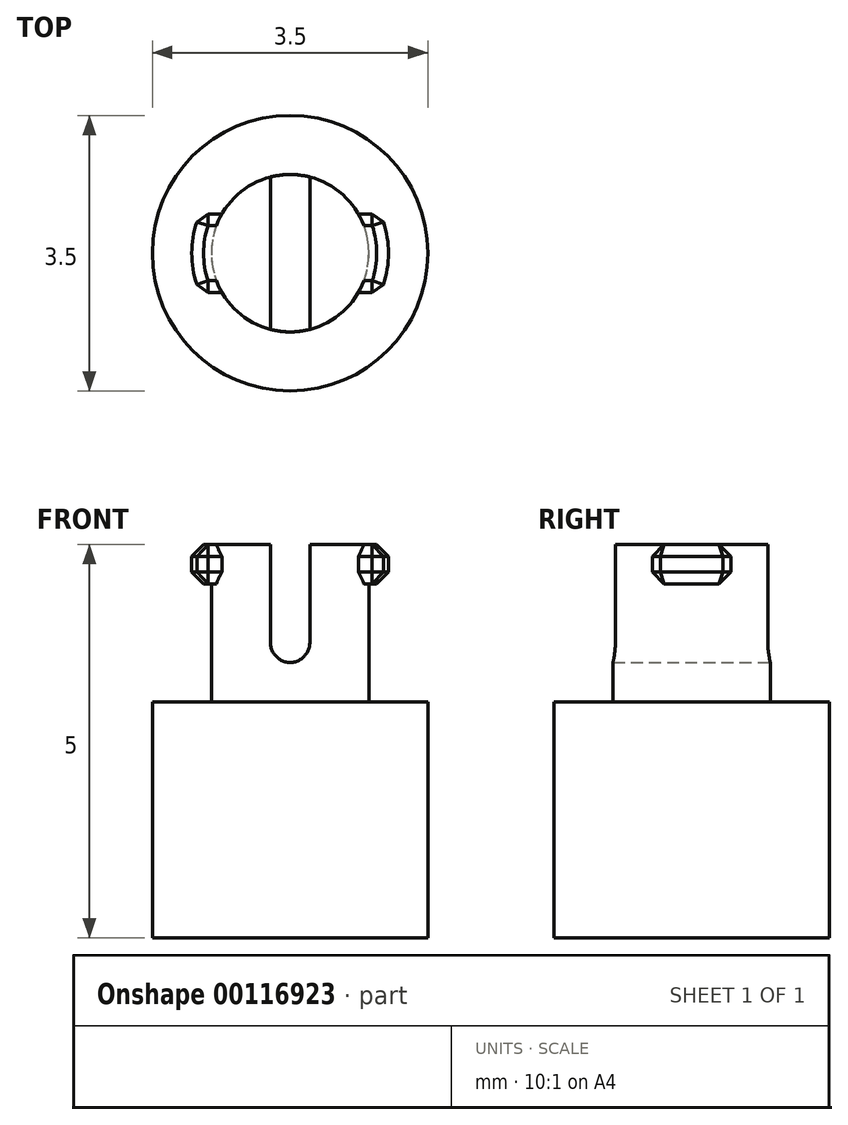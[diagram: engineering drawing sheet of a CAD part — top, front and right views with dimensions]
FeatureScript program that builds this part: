
annotation { "Feature Type Name" : "Feature", "Feature Type Description" : "" }
export const myFeature = defineFeature(function(context is Context, id is Id, definition is map)
    precondition{}
    {
        {
            var Q0;
            Q0=qCreatedBy(makeId("Top.planeOp"),FACE);
            var sketch = newSketch(context, id + "F0", { "sketchPlane" : qUnion([Q0])});
            skCircle(sketch, "E0", {"center": v(0, 0) * mm, "radius": 1 * mm});
            skCircle(sketch, "E1", {"center": v(0, 0) * mm, "radius": 1.75 * mm});
            skSolve(sketch);
        }
        {
            var Q0;
            Q0=makeQuery(id+"F0.imprint","IMPRINT",FACE,{"disambiguationData":[TD([[makeQuery(id+"F0.imprint","IMPRINT",EDGE,{"derivedFrom":sQuery(id+"F0.wireOp",EDGE,"E0")}),-1.0]])]});
            extrude(context, id + "F1", {"entities" : qUnion([Q0]), "depth" : 3 * mm});
        }
        {
            var Q0;
            Q0=makeQuery(id+"F0.imprint","IMPRINT",FACE,{"disambiguationData":[TD([[makeQuery(id+"F0.imprint","IMPRINT",EDGE,{"derivedFrom":sQuery(id+"F0.wireOp",EDGE,"E0")}),1.0]])]});
            extrude(context, id + "F2", {"entities" : qUnion([Q0]), "operationType" : NewBodyOperationType.ADD, "depth" : 5 * mm});
        }
        {
            var Q0;
            {var subQ0=sQuery(id+"F0.wireOp",EDGE,"E0");Q0=makeQuery(id+"F7.boolean.opBoolean","SPLIT",FACE,{"disambiguationData":[TD([makeQuery(id+"F7.opExtrude","SWEPT_FACE",FACE,{"disambiguationData":[OSD([sQuery(id+"F4.wireOp",EDGE,"E6.left")])]})])],"derivedFrom":makeQuery(id+"F2.opExtrude","CAP_FACE",FACE,{"disambiguationData":[OSD([subQ0])],"isStart":false})});}
            var sketch = newSketch(context, id + "F3", { "sketchPlane" : qUnion([Q0])});
            skArc(sketch, "E2", {"start": v(1.15, -0.5) * mm, "mid": v(1.25, 0) * mm, "end": v(1.15, 0.5) * mm});
            skLineSegment(sketch, "E3.bottom", {"start": v(-1.15, -0.5) * mm, "end": v(1.15, -0.5) * mm});
            skLineSegment(sketch, "E3.top", {"start": v(-1.15, 0.5) * mm, "end": v(1.15, 0.5) * mm});
            skArc(sketch, "E4.trimOffspring", {"start": v(-1.15, 0.5) * mm, "mid": v(-1.25, 0) * mm, "end": v(-1.15, -0.5) * mm});
            skPoint(sketch, "E3.left.end.orphan", {"position": v(-1.5, 0.5) * mm});
            skPoint(sketch, "E5.orphan", {"position": v(-1.5, -0.5) * mm});
            skPoint(sketch, "E3.right.end.orphan", {"position": v(1.5, 0.5) * mm});
            skPoint(sketch, "E3.right.start.orphan", {"position": v(1.5, -0.5) * mm});
            skSolve(sketch);
        }
        {
            var Q0;
            Q0=qCreatedBy(makeId("Top.planeOp"),FACE);
            var sketch = newSketch(context, id + "F4", { "sketchPlane" : qUnion([Q0])});
            skLineSegment(sketch, "E6.bottom", {"start": v(-0.25, 2.5) * mm, "end": v(0.25, 2.5) * mm});
            skLineSegment(sketch, "E6.top", {"start": v(-0.25, -2.5) * mm, "end": v(0.25, -2.5) * mm});
            skLineSegment(sketch, "E6.left", {"start": v(-0.25, 2.5) * mm, "end": v(-0.25, -2.5) * mm});
            skLineSegment(sketch, "E6.right", {"start": v(0.25, 2.5) * mm, "end": v(0.25, -2.5) * mm});
            skPoint(sketch, "E6.middle", {"position": v(0, 0) * mm});
            skSolve(sketch);
        }
        {
            var Q0;
            Q0 = qSketchRegion(id + "F3", true);
            extrude(context, id + "F5", {"entities" : qUnion([Q0]), "operationType" : NewBodyOperationType.ADD, "oppositeDirection" : true, "depth" : 0.5 * mm});
        }
        {
            var Q0;
            Q0=makeQuery(id+"F5.opExtrude","CAP_EDGE",EDGE,{"disambiguationData":[OSD([sQuery(id+"F3.wireOp",EDGE,"E4.trimOffspring")])],"isStart":false});
            var Q1;
            {var subQ0=sQuery(id+"F3.wireOp",EDGE,"E4.trimOffspring");var subQ1=sQuery(id+"F3.wireOp",EDGE,"E3.top");Q1=makeQuery(id+"F5.boolean.opBoolean","SPLIT",EDGE,{"disambiguationData":[TD([makeQuery(id+"F5.opExtrude","SWEPT_FACE",FACE,{"disambiguationData":[OSD([subQ0])]})])],"derivedFrom":makeQuery(id+"F5.opExtrude","CAP_EDGE",EDGE,{"disambiguationData":[OSD([subQ1])],"isStart":false})});}
            var Q2;
            {var subQ0=sQuery(id+"F3.wireOp",EDGE,"E4.trimOffspring");var subQ1=sQuery(id+"F3.wireOp",EDGE,"E3.bottom");Q2=makeQuery(id+"F5.boolean.opBoolean","SPLIT",EDGE,{"disambiguationData":[TD([makeQuery(id+"F5.opExtrude","SWEPT_FACE",FACE,{"disambiguationData":[OSD([subQ0])]})])],"derivedFrom":makeQuery(id+"F5.opExtrude","CAP_EDGE",EDGE,{"disambiguationData":[OSD([subQ1])],"isStart":false})});}
            var Q3;
            Q3=makeQuery(id+"F5.opExtrude","SWEPT_EDGE",EDGE,{"disambiguationData":[OSD([sQuery(id+"F3.wireOp",EDGE,"E3.top"),sQuery(id+"F3.wireOp",EDGE,"E4.trimOffspring")])]});
            var Q4;
            Q4=makeQuery(id+"F5.opExtrude","SWEPT_EDGE",EDGE,{"disambiguationData":[OSD([sQuery(id+"F3.wireOp",EDGE,"E3.bottom"),sQuery(id+"F3.wireOp",EDGE,"E4.trimOffspring")])]});
            var Q5;
            Q5=makeQuery(id+"F5.opExtrude","CAP_EDGE",EDGE,{"disambiguationData":[OSD([sQuery(id+"F3.wireOp",EDGE,"E2")])],"isStart":false});
            var Q6;
            Q6=makeQuery(id+"F5.opExtrude","SWEPT_EDGE",EDGE,{"disambiguationData":[OSD([sQuery(id+"F3.wireOp",EDGE,"E2"),sQuery(id+"F3.wireOp",EDGE,"E3.top")])]});
            var Q7;
            {var subQ0=sQuery(id+"F3.wireOp",EDGE,"E2");var subQ1=sQuery(id+"F3.wireOp",EDGE,"E3.top");Q7=makeQuery(id+"F5.boolean.opBoolean","SPLIT",EDGE,{"disambiguationData":[TD([makeQuery(id+"F5.opExtrude","SWEPT_FACE",FACE,{"disambiguationData":[OSD([subQ0])]})])],"derivedFrom":makeQuery(id+"F5.opExtrude","CAP_EDGE",EDGE,{"disambiguationData":[OSD([subQ1])],"isStart":false})});}
            var Q8;
            Q8=makeQuery(id+"F5.opExtrude","SWEPT_EDGE",EDGE,{"disambiguationData":[OSD([sQuery(id+"F3.wireOp",EDGE,"E2"),sQuery(id+"F3.wireOp",EDGE,"E3.bottom")])]});
            var Q9;
            {var subQ0=sQuery(id+"F3.wireOp",EDGE,"E2");var subQ1=sQuery(id+"F3.wireOp",EDGE,"E3.bottom");Q9=makeQuery(id+"F5.boolean.opBoolean","SPLIT",EDGE,{"disambiguationData":[TD([makeQuery(id+"F5.opExtrude","SWEPT_FACE",FACE,{"disambiguationData":[OSD([subQ0])]})])],"derivedFrom":makeQuery(id+"F5.opExtrude","CAP_EDGE",EDGE,{"disambiguationData":[OSD([subQ1])],"isStart":false})});}
            var Q10;
            Q10=makeQuery(id+"F5.opExtrude","CAP_EDGE",EDGE,{"disambiguationData":[OSD([sQuery(id+"F3.wireOp",EDGE,"E4.trimOffspring")])],"isStart":true});
            var Q11;
            Q11=makeQuery(id+"F5.opExtrude","CAP_EDGE",EDGE,{"disambiguationData":[OSD([sQuery(id+"F3.wireOp",EDGE,"E2")])],"isStart":true});
            var Q12;
            {var subQ0=sQuery(id+"F3.wireOp",EDGE,"E3.bottom");var subQ1=sQuery(id+"F3.wireOp",EDGE,"E2");Q12=makeQuery(id+"F5.boolean.opBoolean","SPLIT",EDGE,{"disambiguationData":[TD([makeQuery(id+"F5.opExtrude","SWEPT_FACE",FACE,{"disambiguationData":[OSD([subQ1])]})])],"derivedFrom":makeQuery(id+"F5.opExtrude","CAP_EDGE",EDGE,{"disambiguationData":[OSD([subQ0])],"isStart":true})});}
            var Q13;
            {var subQ0=sQuery(id+"F3.wireOp",EDGE,"E3.bottom");var subQ1=sQuery(id+"F3.wireOp",EDGE,"E4.trimOffspring");Q13=makeQuery(id+"F5.boolean.opBoolean","SPLIT",EDGE,{"disambiguationData":[TD([makeQuery(id+"F5.opExtrude","SWEPT_FACE",FACE,{"disambiguationData":[OSD([subQ1])]})])],"derivedFrom":makeQuery(id+"F5.opExtrude","CAP_EDGE",EDGE,{"disambiguationData":[OSD([subQ0])],"isStart":true})});}
            var Q14;
            {var subQ0=sQuery(id+"F3.wireOp",EDGE,"E3.top");var subQ2=sQuery(id+"F3.wireOp",EDGE,"E4.trimOffspring");Q14=makeQuery(id+"F5.boolean.opBoolean","SPLIT",EDGE,{"disambiguationData":[TD([makeQuery(id+"F5.opExtrude","SWEPT_FACE",FACE,{"disambiguationData":[OSD([subQ2])]})])],"derivedFrom":makeQuery(id+"F5.opExtrude","CAP_EDGE",EDGE,{"disambiguationData":[OSD([subQ0])],"isStart":true})});}
            var Q15;
            {var subQ0=sQuery(id+"F3.wireOp",EDGE,"E3.top");var subQ1=sQuery(id+"F3.wireOp",EDGE,"E2");Q15=makeQuery(id+"F5.boolean.opBoolean","SPLIT",EDGE,{"disambiguationData":[TD([makeQuery(id+"F5.opExtrude","SWEPT_FACE",FACE,{"disambiguationData":[OSD([subQ1])]})])],"derivedFrom":makeQuery(id+"F5.opExtrude","CAP_EDGE",EDGE,{"disambiguationData":[OSD([subQ0])],"isStart":true})});}
            chamfer(context, id + "F6", {"entities" : qUnion([Q0, Q1, Q2, Q3, Q4, Q5, Q6, Q7, Q8, Q9, Q10, Q11, Q12, Q13, Q14, Q15]), "width" : 0.15 * mm});
        }
        {
            var Q0;
            Q0=makeQuery(id+"F4.imprint","IMPRINT",FACE,{"disambiguationData":[TD([[makeQuery(id+"F4.imprint","IMPRINT",EDGE,{"derivedFrom":sQuery(id+"F4.wireOp",EDGE,"E6.bottom")}),-1.0]])]});
            extrude(context, id + "F7", {"entities" : qUnion([Q0]), "operationType" : NewBodyOperationType.REMOVE, "depth" : 25 * mm, "hasSecondDirection" : true, "secondDirectionOppositeDirection" : false, "secondDirectionDepth" : 3.5 * mm});
        }
        {
            var Q0;
            Q0=makeQuery(id+"F7.boolean.opBoolean","COPY",EDGE,{"derivedFrom":makeQuery(id+"F7.opExtrude","CAP_EDGE",EDGE,{"disambiguationData":[OSD([sQuery(id+"F4.wireOp",EDGE,"E6.left")])],"isStart":true})});
            var Q1;
            Q1=makeQuery(id+"F7.boolean.opBoolean","COPY",EDGE,{"derivedFrom":makeQuery(id+"F7.opExtrude","CAP_EDGE",EDGE,{"disambiguationData":[OSD([sQuery(id+"F4.wireOp",EDGE,"E6.right")])],"isStart":true})});
            fillet(context, id + "F8", {"entities" : qUnion([Q0, Q1]), "radius" : 0.25 * mm, "tangentPropagation" : true, "allowEdgeOverflow" : false});
        }
    });
